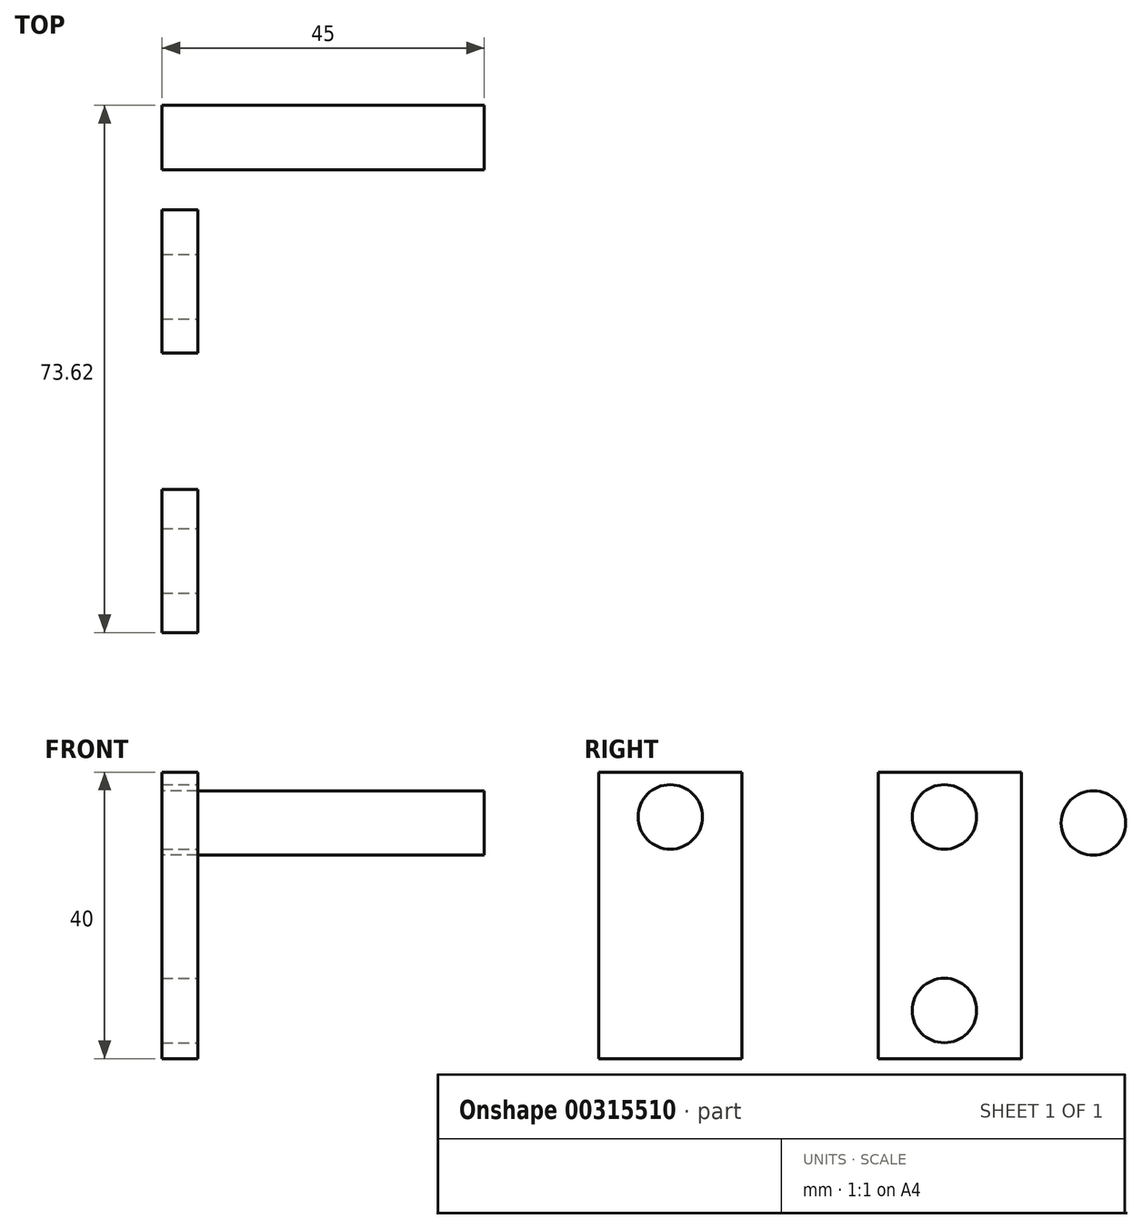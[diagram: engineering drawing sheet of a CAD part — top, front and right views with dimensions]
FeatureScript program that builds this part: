
annotation { "Feature Type Name" : "Feature", "Feature Type Description" : "" }
export const myFeature = defineFeature(function(context is Context, id is Id, definition is map)
    precondition{}
    {
        {
            var Q0;
            Q0=qCreatedBy(makeId("Right.planeOp"),FACE);
            var sketch = newSketch(context, id + "F0", { "sketchPlane" : qUnion([Q0])});
            skLineSegment(sketch, "E0.bottom", {"start": v(8.25, 40) * mm, "end": v(28.25, 40) * mm});
            skLineSegment(sketch, "E0.top", {"start": v(8.25, 0) * mm, "end": v(28.25, 0) * mm});
            skLineSegment(sketch, "E0.left", {"start": v(8.25, 40) * mm, "end": v(8.25, 0) * mm});
            skLineSegment(sketch, "E0.right", {"start": v(28.25, 40) * mm, "end": v(28.25, 0) * mm});
            skLineSegment(sketch, "E1.bottom", {"start": v(-10.79, 40) * mm, "end": v(-30.79, 40) * mm});
            skLineSegment(sketch, "E1.top", {"start": v(-10.79, 0) * mm, "end": v(-30.79, 0) * mm});
            skLineSegment(sketch, "E1.left", {"start": v(-10.79, 40) * mm, "end": v(-10.79, 0) * mm});
            skLineSegment(sketch, "E1.right", {"start": v(-30.79, 40) * mm, "end": v(-30.79, 0) * mm});
            skSolve(sketch);
        }
        {
            var Q0;
            Q0=makeQuery(id+"F0.imprint","IMPRINT",FACE,{"disambiguationData":[TD([[makeQuery(id+"F0.imprint","IMPRINT",EDGE,{"derivedFrom":sQuery(id+"F0.wireOp",EDGE,"E1.bottom")}),1.0]])]});
            var Q1;
            Q1=makeQuery(id+"F0.imprint","IMPRINT",FACE,{"disambiguationData":[TD([[makeQuery(id+"F0.imprint","IMPRINT",EDGE,{"derivedFrom":sQuery(id+"F0.wireOp",EDGE,"E0.bottom")}),-1.0]])]});
            extrude(context, id + "F1", {"entities" : qUnion([Q0, Q1]), "depth" : 5 * mm});
        }
        {
            var Q0;
            Q0=makeQuery(id+"F1.opExtrude","CAP_FACE",FACE,{"disambiguationData":[OSD([sQuery(id+"F0.wireOp",EDGE,"E1.bottom"),sQuery(id+"F0.wireOp",EDGE,"E1.top"),sQuery(id+"F0.wireOp",EDGE,"E1.left"),sQuery(id+"F0.wireOp",EDGE,"E1.right")])],"isStart":false});
            var sketch = newSketch(context, id + "F2", { "sketchPlane" : qUnion([Q0])});
            skCircle(sketch, "E2", {"center": v(-20.79, 33.75) * mm, "radius": 4.5 * mm});
            skPoint(sketch, "E2.centerSnap0", {"position": v(-20.79, 40) * mm});
            skSolve(sketch);
        }
        {
            var Q0;
            Q0=makeQuery(id+"F2.imprint","IMPRINT",FACE,{"disambiguationData":[TD([[makeQuery(id+"F2.imprint","IMPRINT",EDGE,{"derivedFrom":sQuery(id+"F2.wireOp",EDGE,"E2")}),1.0]])]});
            var Q1;
            Q1=sQuery(id+"F2.wireOp",EDGE,"E2");
            extrude(context, id + "F3", {"entities" : qUnion([Q0]), "operationType" : NewBodyOperationType.REMOVE, "surfaceEntities" : qUnion([Q1]), "oppositeDirection" : true, "depth" : 30 * mm});
        }
        {
            var Q0;
            Q0=makeQuery(id+"F1.opExtrude","CAP_FACE",FACE,{"disambiguationData":[OSD([sQuery(id+"F0.wireOp",EDGE,"E0.bottom"),sQuery(id+"F0.wireOp",EDGE,"E0.top"),sQuery(id+"F0.wireOp",EDGE,"E0.left"),sQuery(id+"F0.wireOp",EDGE,"E0.right")])],"isStart":false});
            var sketch = newSketch(context, id + "F4", { "sketchPlane" : qUnion([Q0])});
            skCircle(sketch, "E3", {"center": v(17.5, 33.75) * mm, "radius": 4.5 * mm});
            skCircle(sketch, "E4", {"center": v(17.5, 6.7) * mm, "radius": 4.5 * mm});
            skSolve(sketch);
        }
        {
            var Q0;
            Q0=makeQuery(id+"F4.imprint","IMPRINT",FACE,{"disambiguationData":[TD([[makeQuery(id+"F4.imprint","IMPRINT",EDGE,{"derivedFrom":sQuery(id+"F4.wireOp",EDGE,"E3")}),1.0]])]});
            var Q1;
            Q1=makeQuery(id+"F4.imprint","IMPRINT",FACE,{"disambiguationData":[TD([[makeQuery(id+"F4.imprint","IMPRINT",EDGE,{"derivedFrom":sQuery(id+"F4.wireOp",EDGE,"E4")}),1.0]])]});
            var Q2;
            Q2=sQuery(id+"F4.wireOp",EDGE,"E3");
            extrude(context, id + "F5", {"entities" : qUnion([Q0, Q1]), "operationType" : NewBodyOperationType.REMOVE, "surfaceEntities" : qUnion([Q2]), "oppositeDirection" : true, "depth" : 30 * mm});
        }
        {
            var Q0;
            Q0=qCreatedBy(makeId("Right.planeOp"),FACE);
            var sketch = newSketch(context, id + "F6", { "sketchPlane" : qUnion([Q0])});
            skCircle(sketch, "E5", {"center": v(38.33, 32.9) * mm, "radius": 4.5 * mm});
            skSolve(sketch);
        }
        {
            var Q0;
            Q0 = qSketchRegion(id + "F6", true);
            extrude(context, id + "F7", {"entities" : qUnion([Q0]), "depth" : 45 * mm});
        }
    });
